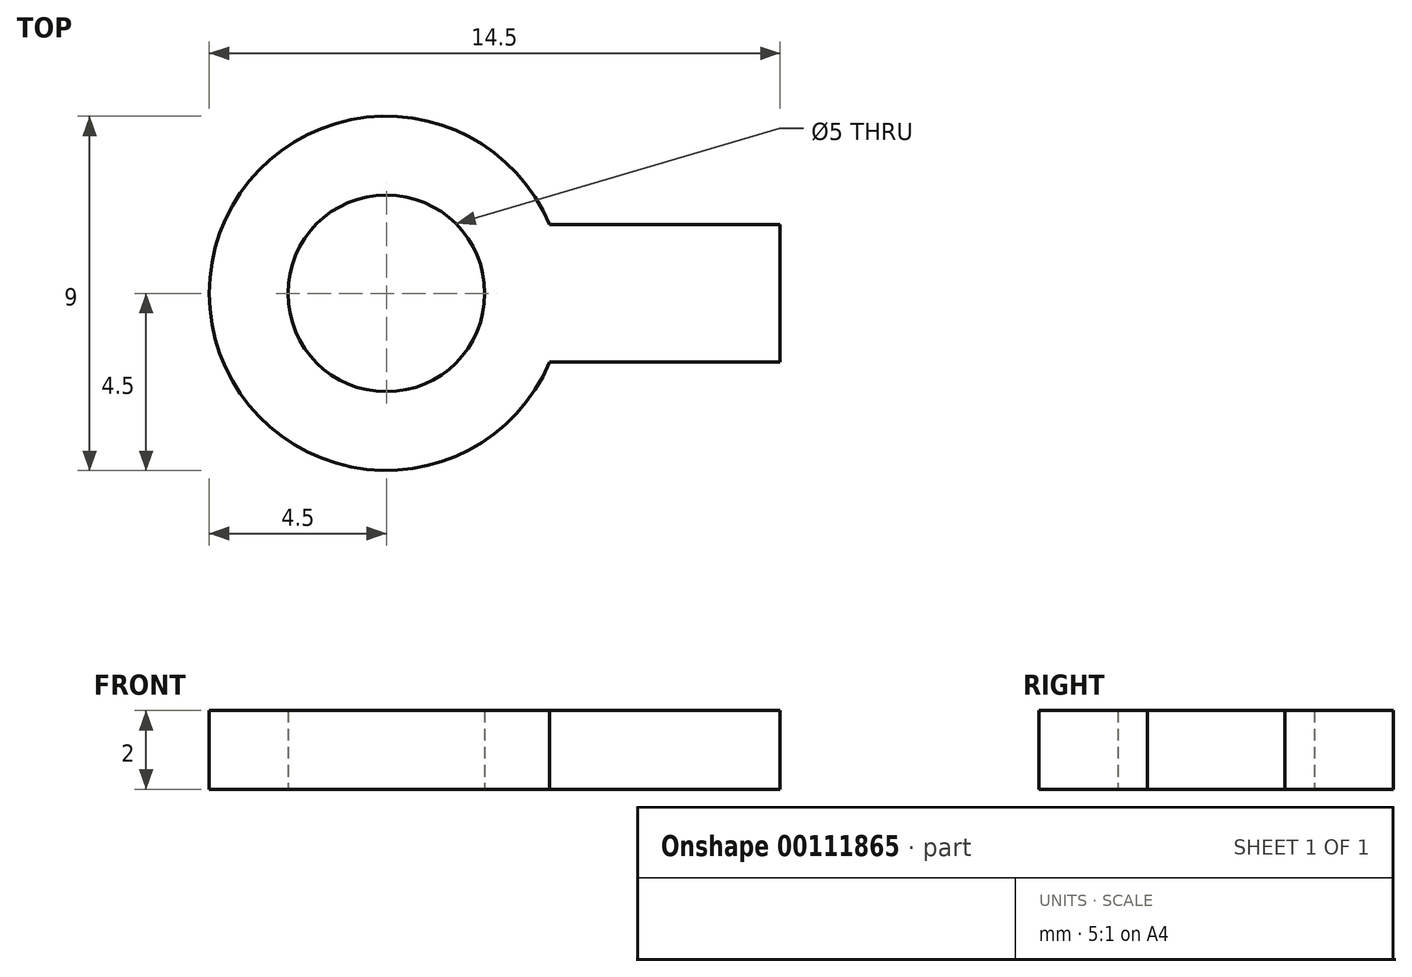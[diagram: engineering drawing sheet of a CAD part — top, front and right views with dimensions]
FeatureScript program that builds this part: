
annotation { "Feature Type Name" : "Feature", "Feature Type Description" : "" }
export const myFeature = defineFeature(function(context is Context, id is Id, definition is map)
    precondition{}
    {
        {
            var Q0;
            Q0=qCreatedBy(makeId("Top.planeOp"),FACE);
            var sketch = newSketch(context, id + "F0", { "sketchPlane" : qUnion([Q0])});
            skCircle(sketch, "E0", {"center": v(0, 0) * mm, "radius": 2.5 * mm});
            skArc(sketch, "E1", {"start": v(4.15, 1.75) * mm, "mid": v(-4.5, 0) * mm, "end": v(4.15, -1.75) * mm});
            skLineSegment(sketch, "E2", {"start": v(4.15, 1.75) * mm, "end": v(10, 1.75) * mm});
            skLineSegment(sketch, "E3", {"start": v(10, 1.75) * mm, "end": v(10, -1.75) * mm});
            skLineSegment(sketch, "E4", {"start": v(10, -1.75) * mm, "end": v(4.15, -1.75) * mm});
            skSolve(sketch);
        }
        {
            var Q0;
            Q0=makeQuery(id+"F0.imprint","IMPRINT",FACE,{"disambiguationData":[TD([[makeQuery(id+"F0.imprint","IMPRINT",EDGE,{"derivedFrom":sQuery(id+"F0.wireOp",EDGE,"E0")}),-1.0]])]});
            extrude(context, id + "F1", {"entities" : qUnion([Q0]), "depth" : 2 * mm});
        }
    });
